# Revit family: Seating-Lounge-Bernhardt_Design-Vika
name_source: partatom
category: Furniture
revit_build: Autodesk Revit Architecture 2013 (Build: 20130531_2115(x64)
units: mm (PartAtom-declared; Revit-internal decimal feet)

## types (2) — shared parameters
Depth = 2' - 9 3/8"
Description = Lounge
Height = 2' - 10"
Manufacturer = Bernhardt Design
Metal Finish = Metal - Bernhardt Design - Polished Stainless Steel
Product Documentation Link = http://www.bernhardtdesign.com
Product Name = Vika
Product Page URL = http://www.bernhardtdesign.com
Seat Finish = Fabric- Bernhardt Design - Red Linen
Seat Height = 1' - 1 7/8"
URL = http://www.bernhardtdesign.com
Width = 2' - 9"

## per-type parameters (varying)
| type | Shell Finish |
| 4700 | Fabric- Bernhardt Design - Red Linen |
| 4701 | Fiberglass - Bernhardt Design - White |

note: column(s) folded — value = type name in every type: Model

## geometry (parser evidence)
native form markers: Blend x53, Sweep x4
no freeform markers — native parametric forms only
